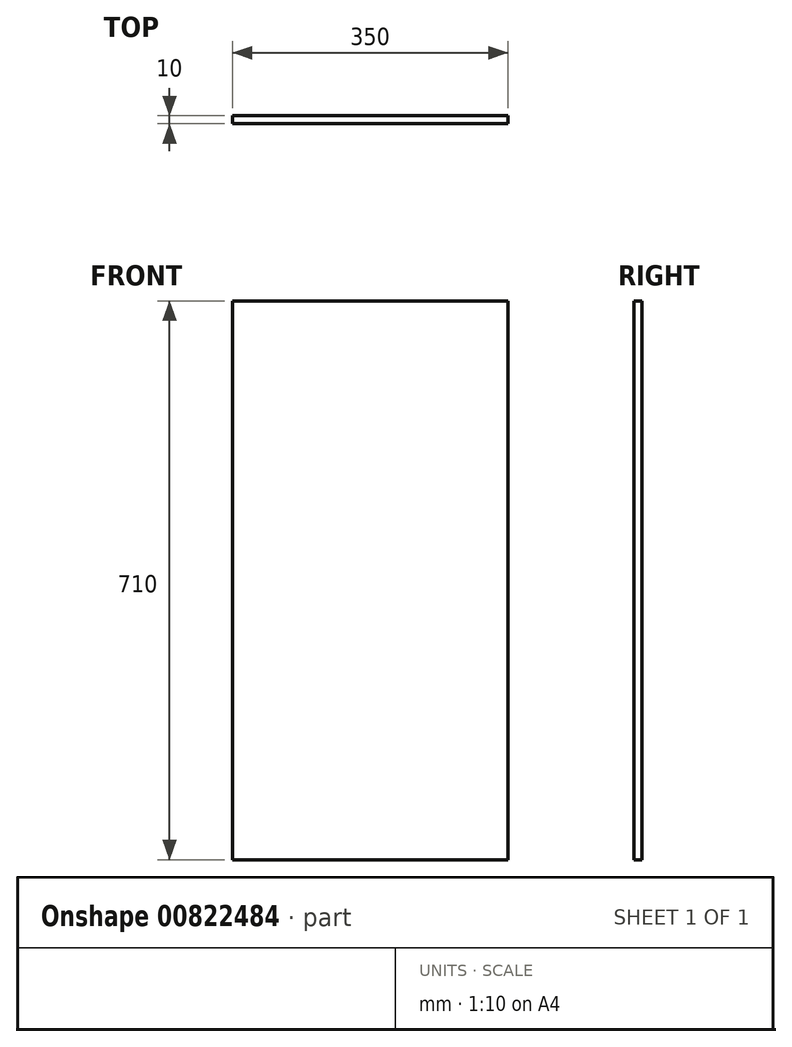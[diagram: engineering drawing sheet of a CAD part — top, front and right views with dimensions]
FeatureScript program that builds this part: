
annotation { "Feature Type Name" : "Feature", "Feature Type Description" : "" }
export const myFeature = defineFeature(function(context is Context, id is Id, definition is map)
    precondition{}
    {
        {
            var Q0;
            Q0=qCreatedBy(makeId("Front.planeOp"),FACE);
            var sketch = newSketch(context, id + "F0", { "sketchPlane" : qUnion([Q0])});
            skLineSegment(sketch, "E0.bottom", {"start": v(-235.58, 496.13) * mm, "end": v(114.42, 496.13) * mm});
            skLineSegment(sketch, "E0.top", {"start": v(-235.58, -213.87) * mm, "end": v(114.42, -213.87) * mm});
            skLineSegment(sketch, "E0.left", {"start": v(-235.58, 496.13) * mm, "end": v(-235.58, -213.87) * mm});
            skLineSegment(sketch, "E0.right", {"start": v(114.42, 496.13) * mm, "end": v(114.42, -213.87) * mm});
            skSolve(sketch);
        }
        {
            var Q0;
            Q0=makeQuery(id+"F0.imprint","IMPRINT",FACE,{"disambiguationData":[TD([[makeQuery(id+"F0.imprint","IMPRINT",EDGE,{"derivedFrom":sQuery(id+"F0.wireOp",EDGE,"E0.bottom")}),-1.0]])]});
            extrude(context, id + "F1", {"entities" : qUnion([Q0]), "depth" : 10 * mm, "offsetDistance" : 25.4 * mm});
        }
    });
